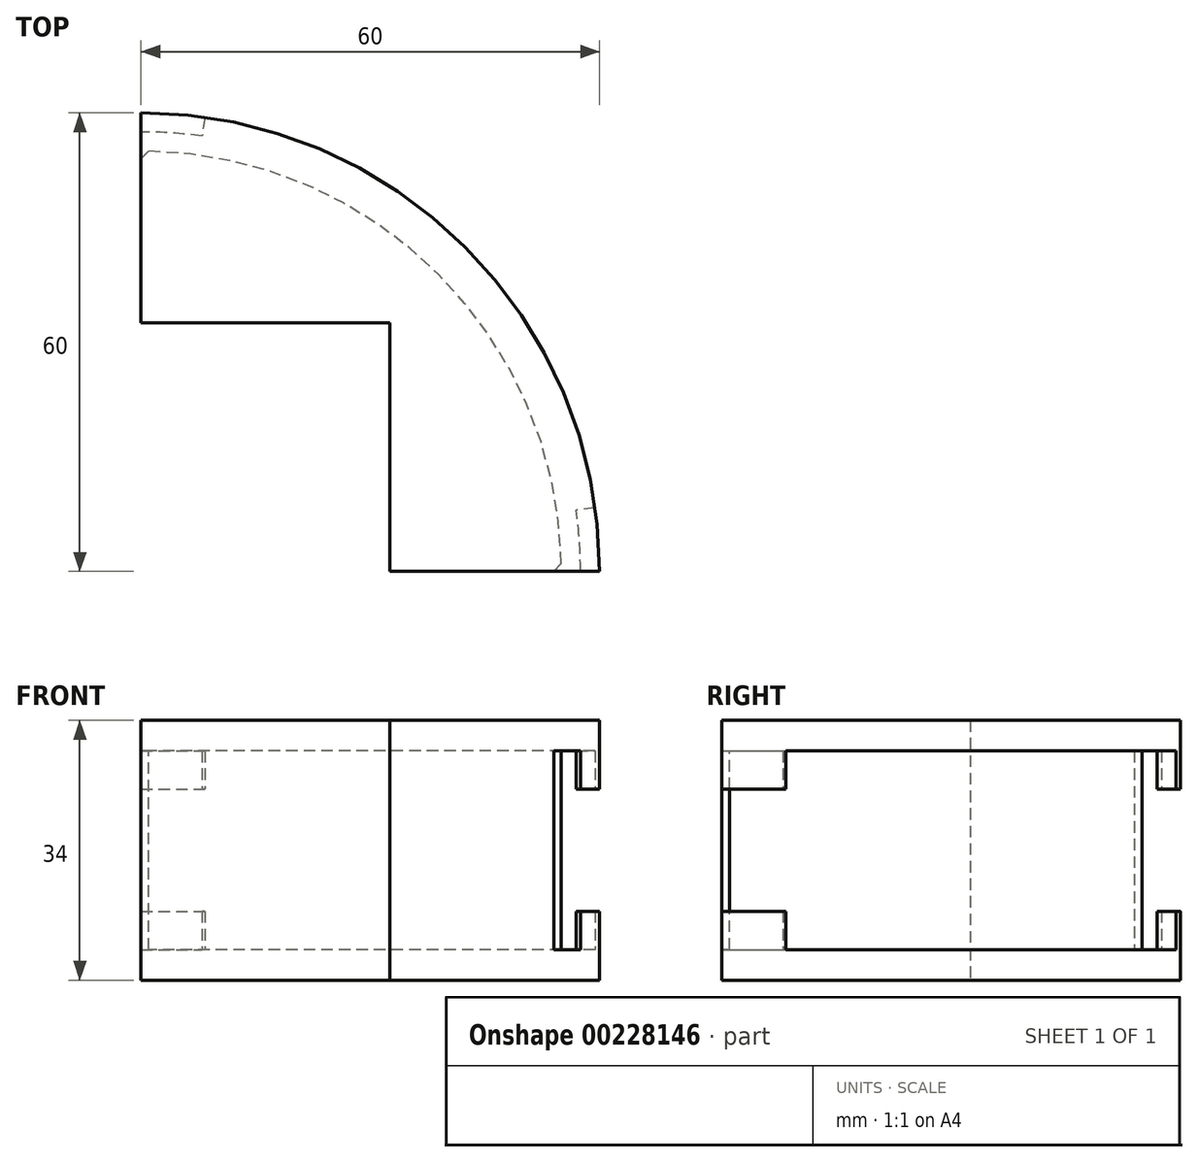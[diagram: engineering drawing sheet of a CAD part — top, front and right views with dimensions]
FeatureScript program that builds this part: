
annotation { "Feature Type Name" : "Feature", "Feature Type Description" : "" }
export const myFeature = defineFeature(function(context is Context, id is Id, definition is map)
    precondition{}
    {
        {
            var Q0;
            Q0=qCreatedBy(makeId("Front.planeOp"),FACE);
            var sketch = newSketch(context, id + "F0", { "sketchPlane" : qUnion([Q0])});
            skLineSegment(sketch, "E0", {"start": v(-50, 4) * mm, "end": v(-50, -30) * mm});
            skLineSegment(sketch, "E1", {"start": v(-50, -30) * mm, "end": v(0, -30) * mm});
            skLineSegment(sketch, "E2", {"start": v(0, -30) * mm, "end": v(0, -26) * mm});
            skLineSegment(sketch, "E3", {"start": v(0, -26) * mm, "end": v(-5, -26) * mm});
            skLineSegment(sketch, "E4", {"start": v(-5, -26) * mm, "end": v(-5, 0) * mm});
            skLineSegment(sketch, "E5", {"start": v(-5, 0) * mm, "end": v(0, 0) * mm});
            skLineSegment(sketch, "E6", {"start": v(0, 0) * mm, "end": v(0, 4) * mm});
            skLineSegment(sketch, "E7", {"start": v(0, 4) * mm, "end": v(-50, 4) * mm});
            skSolve(sketch);
        }
        {
            var Q0;
            Q0=qCreatedBy(makeId("Top.planeOp"),FACE);
            var sketch = newSketch(context, id + "F1", { "sketchPlane" : qUnion([Q0])});
            skArc(sketch, "E8", {"start": v(0, 0) * mm, "mid": v(-17.57, 42.43) * mm, "end": v(-60, 60) * mm});
            skLineSegment(sketch, "E9.bottom", {"start": v(-60, 0) * mm, "end": v(-27.47, 0) * mm});
            skLineSegment(sketch, "E9.top", {"start": v(-60, 32.53) * mm, "end": v(-27.47, 32.53) * mm});
            skLineSegment(sketch, "E9.left", {"start": v(-60, 0) * mm, "end": v(-60, 32.53) * mm});
            skLineSegment(sketch, "E9.right", {"start": v(-27.47, 0) * mm, "end": v(-27.47, 32.53) * mm});
            skArc(sketch, "E10", {"start": v(-30.47, 32.53) * mm, "mid": v(-25.35, 34.65) * mm, "end": v(-27.47, 29.53) * mm});
            skArc(sketch, "E11", {"start": v(-2.5, 0) * mm, "mid": v(-2.64, 4) * mm, "end": v(-3.06, 8) * mm});
            skArc(sketch, "E12", {"start": v(-60, 57.5) * mm, "mid": v(-56, 57.36) * mm, "end": v(-52, 56.94) * mm});
            skSolve(sketch);
        }
        {
            var Q0;
            Q0=makeQuery(id+"F0.imprint","IMPRINT",FACE,{"disambiguationData":[TD([[makeQuery(id+"F0.imprint","IMPRINT",EDGE,{"derivedFrom":sQuery(id+"F0.wireOp",EDGE,"E0")}),1.0]])]});
            var Q1;
            Q1=sQuery(id+"F1.wireOp",EDGE,"E8");
            sweep(context, id + "F2", {"profiles" : qUnion([Q0]), "path" : qUnion([Q1])});
        }
        {
            var Q0;
            {var subQ3=sQuery(id+"F1.wireOp",EDGE,"E10");Q0=makeQuery(id+"F1.imprint","IMPRINT",FACE,{"disambiguationData":[TD([[makeQuery(id+"F1.imprint","IMPRINT",EDGE,{"derivedFrom":subQ3}),-1.0]])]});}
            var Q1;
            {var subQ7=sQuery(id+"F1.wireOp",EDGE,"E9.bottom");Q1=makeQuery(id+"F1.imprint","IMPRINT",FACE,{"disambiguationData":[TD([[makeQuery(id+"F1.imprint","IMPRINT",EDGE,{"derivedFrom":subQ7}),1.0]])]});}
            extrude(context, id + "F3", {"entities" : qUnion([Q0, Q1]), "operationType" : NewBodyOperationType.REMOVE, "endBound" : BoundingType.SYMMETRIC, "depth" : 135.2 * mm});
        }
        {
            var Q0;
            Q0=makeQuery(id+"F2.opSweep","CAP_FACE",FACE,{"disambiguationData":[OSD([sQuery(id+"F0.wireOp",EDGE,"E0"),sQuery(id+"F0.wireOp",EDGE,"E1"),sQuery(id+"F0.wireOp",EDGE,"E2"),sQuery(id+"F0.wireOp",EDGE,"E3"),sQuery(id+"F0.wireOp",EDGE,"E4"),sQuery(id+"F0.wireOp",EDGE,"E5"),sQuery(id+"F0.wireOp",EDGE,"E6"),sQuery(id+"F0.wireOp",EDGE,"E7"),sQuery(id+"F1.wireOp",VERTEX,"E8.end")])],"isStart":false});
            var sketch = newSketch(context, id + "F4", { "sketchPlane" : qUnion([Q0])});
            skLineSegment(sketch, "E13.bottom", {"start": v(-60, 0) * mm, "end": v(-57.5, 0) * mm});
            skLineSegment(sketch, "E13.top", {"start": v(-60, -5) * mm, "end": v(-57.5, -5) * mm});
            skLineSegment(sketch, "E13.left", {"start": v(-60, 0) * mm, "end": v(-60, -5) * mm});
            skLineSegment(sketch, "E13.right", {"start": v(-57.5, 0) * mm, "end": v(-57.5, -5) * mm});
            skLineSegment(sketch, "E14.bottom", {"start": v(-60, -21) * mm, "end": v(-57.5, -21) * mm});
            skLineSegment(sketch, "E14.top", {"start": v(-60, -26) * mm, "end": v(-57.5, -26) * mm});
            skLineSegment(sketch, "E14.left", {"start": v(-60, -21) * mm, "end": v(-60, -26) * mm});
            skLineSegment(sketch, "E14.right", {"start": v(-57.5, -21) * mm, "end": v(-57.5, -26) * mm});
            skSolve(sketch);
        }
        {
            var Q0;
            Q0=makeQuery(id+"F4.imprint","IMPRINT",FACE,{"disambiguationData":[TD([[makeQuery(id+"F4.imprint","IMPRINT",EDGE,{"derivedFrom":sQuery(id+"F4.wireOp",EDGE,"E13.bottom")}),-1.0]])]});
            var Q1;
            Q1=makeQuery(id+"F4.imprint","IMPRINT",FACE,{"disambiguationData":[TD([[makeQuery(id+"F4.imprint","IMPRINT",EDGE,{"derivedFrom":sQuery(id+"F4.wireOp",EDGE,"E14.bottom")}),-1.0]])]});
            var Q2;
            Q2=sQuery(id+"F1.wireOp",EDGE,"E12");
            sweep(context, id + "F5", {"operationType" : NewBodyOperationType.ADD, "profiles" : qUnion([Q0, Q1]), "path" : qUnion([Q2])});
        }
        {
            var Q0;
            Q0=makeQuery(id+"F0.imprint","IMPRINT",FACE,{"disambiguationData":[TD([[makeQuery(id+"F0.imprint","IMPRINT",EDGE,{"derivedFrom":sQuery(id+"F0.wireOp",EDGE,"E0")}),1.0]])]});
            var sketch = newSketch(context, id + "F6", { "sketchPlane" : qUnion([Q0])});
            skLineSegment(sketch, "E15.bottom", {"start": v(0, 0) * mm, "end": v(-2.5, 0) * mm});
            skLineSegment(sketch, "E15.top", {"start": v(0, -5) * mm, "end": v(-2.5, -5) * mm});
            skLineSegment(sketch, "E15.left", {"start": v(0, 0) * mm, "end": v(0, -5) * mm});
            skLineSegment(sketch, "E15.right", {"start": v(-2.5, 0) * mm, "end": v(-2.5, -5) * mm});
            skLineSegment(sketch, "E16.bottom", {"start": v(0, -21) * mm, "end": v(-2.5, -21) * mm});
            skLineSegment(sketch, "E16.top", {"start": v(0, -26) * mm, "end": v(-2.5, -26) * mm});
            skLineSegment(sketch, "E16.left", {"start": v(0, -21) * mm, "end": v(0, -26) * mm});
            skLineSegment(sketch, "E16.right", {"start": v(-2.5, -21) * mm, "end": v(-2.5, -26) * mm});
            skSolve(sketch);
        }
        {
            var Q0;
            Q0=makeQuery(id+"F6.imprint","IMPRINT",FACE,{"disambiguationData":[TD([[makeQuery(id+"F6.imprint","IMPRINT",EDGE,{"derivedFrom":sQuery(id+"F6.wireOp",EDGE,"E15.bottom")}),-1.0]])]});
            var Q1;
            Q1=makeQuery(id+"F6.imprint","IMPRINT",FACE,{"disambiguationData":[TD([[makeQuery(id+"F6.imprint","IMPRINT",EDGE,{"derivedFrom":sQuery(id+"F6.wireOp",EDGE,"E16.bottom")}),1.0]])]});
            var Q2;
            Q2=sQuery(id+"F1.wireOp",EDGE,"E11");
            sweep(context, id + "F7", {"operationType" : NewBodyOperationType.ADD, "profiles" : qUnion([Q0, Q1]), "path" : qUnion([Q2])});
        }
        {
            var Q0;
            Q0=makeQuery(id+"F2.opSweep","CAP_EDGE",EDGE,{"disambiguationData":[OSD([sQuery(id+"F0.wireOp",EDGE,"E4"),sQuery(id+"F1.wireOp",VERTEX,"E8.end")])],"isStart":false});
            var Q1;
            Q1=makeQuery(id+"F2.opSweep","CAP_EDGE",EDGE,{"disambiguationData":[OSD([sQuery(id+"F0.wireOp",EDGE,"E4"),sQuery(id+"F1.wireOp",VERTEX,"E8.start")])],"isStart":true});
            chamfer(context, id + "F8", {"entities" : qUnion([Q0, Q1]), "width" : 1 * mm, "tangentPropagation" : true});
        }
    });
